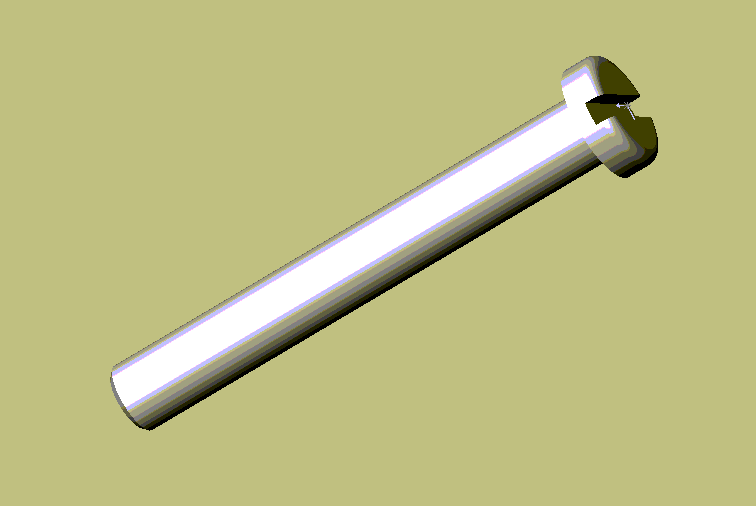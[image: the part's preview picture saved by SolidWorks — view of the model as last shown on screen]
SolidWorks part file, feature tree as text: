
SOLIDWORKS PART (.sldprt)
format: sldprt  version: not decoded by parser v0  size: 125,440 bytes
history: native  units: mm
features: plane x3, sketch x3, extrude x2, material x1, chamfer x1, cut_extrude x1, fillet x1 (+8 scaffold rows collapsed)
feature tree (20):
  scaffold x8  (default folders/planes/origin — collapsed)
  material  "Matériau <non spécifié>"
  plane  "Plane1"
  plane  "Plane2"
  plane  "Plane3"
  sketch  "Esquisse1"  dims[D1=5.0mm]
  extrude  "Base-Extrusion"  Depth=1.5mm
  sketch  "Esquisse2"  dims[D1=3.0mm]
  extrude  "Boss.-Extru.1"  Depth=23mm
  chamfer  "Chanfrein1"  Distance=0.25mm Angle=45deg
  sketch  "Esquisse3"  dims[D1=1.0mm]
  cut_extrude  "Enlèv. mat.-Extru.1"  Depth=0.75mm
  fillet  "Congé1"  Radius=0.5mm
decode coverage: 8 of 8 modeling features carry decoded parameters
note: suppression state not decoded; provenance and decode notes live in map.json
